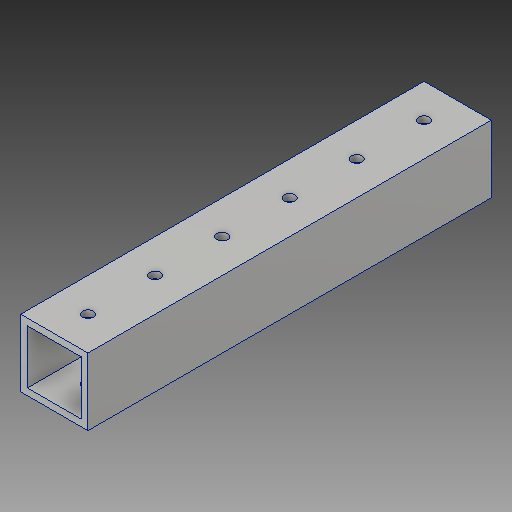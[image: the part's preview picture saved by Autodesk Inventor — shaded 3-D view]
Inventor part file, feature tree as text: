
AUTODESK INVENTOR PART (.ipt)
format: ipt  version: 2018 (Build 220112000, 112)  size: 140,800 bytes
history: native  units: in
note: dims shown in document units (in); Inventor stores cm internally (conversion verified against a paired STEP export)
features: other x5, sketch x3, hole x2, pattern_linear x2, projected_geometry x2, extrude x1
ambient origin geometry x8: Origin, YZ Plane, XZ Plane, XY Plane, X Axis, Y Axis, Z Axis, Center Point
bodies: Solid1 (feature_tree)
feature tree (15):
  other  "Table"
  other  "versatubing_1x1x40-"
  other  "versatubing_1x1x100-"
  other  "versatubing_1x2x100-"
  other  "versatubing_1x2ABS-"
  extrude  "Extrusion1"  Depth=1.0in
  hole  "Hole3"  [1 undecoded]
  hole  "Hole4"  [1 undecoded]
  pattern_linear  "Rectangular Pattern1"  Spacing1=1.0in  [1 undecoded]
  pattern_linear  "Rectangular Pattern2"  Count1=7  [1 undecoded]
  sketch  "Sketch1"  dims[d4=0.0in d5=1.0in]
  sketch  "Sketch2"  dims[d6=0.5in d7=0.5in]
  projected_geometry  "Projected Loop1"
  sketch  "Sketch3"  dims[d22=1.0in d23=0.5in d24=1.0in d39=0.161in d40=0.75in d41=0.375in d42=0.25in d43=0.5635in d44=1.0in d45=0.8108in d46=0.161in d47=0.75in d48=0.375in d49=0.25in d50=0.5635in d51=1.0in d52=0.8108in d53=2.7559in d55=1.0in d56=2.7559in d58=1.0in]
  projected_geometry  "Projected Loop2"
note: 4 required parameter values undecoded (feature->parameter linkage not recoverable at this tier; creation-order binding heuristic only, values carry confidence <= 0.55)
